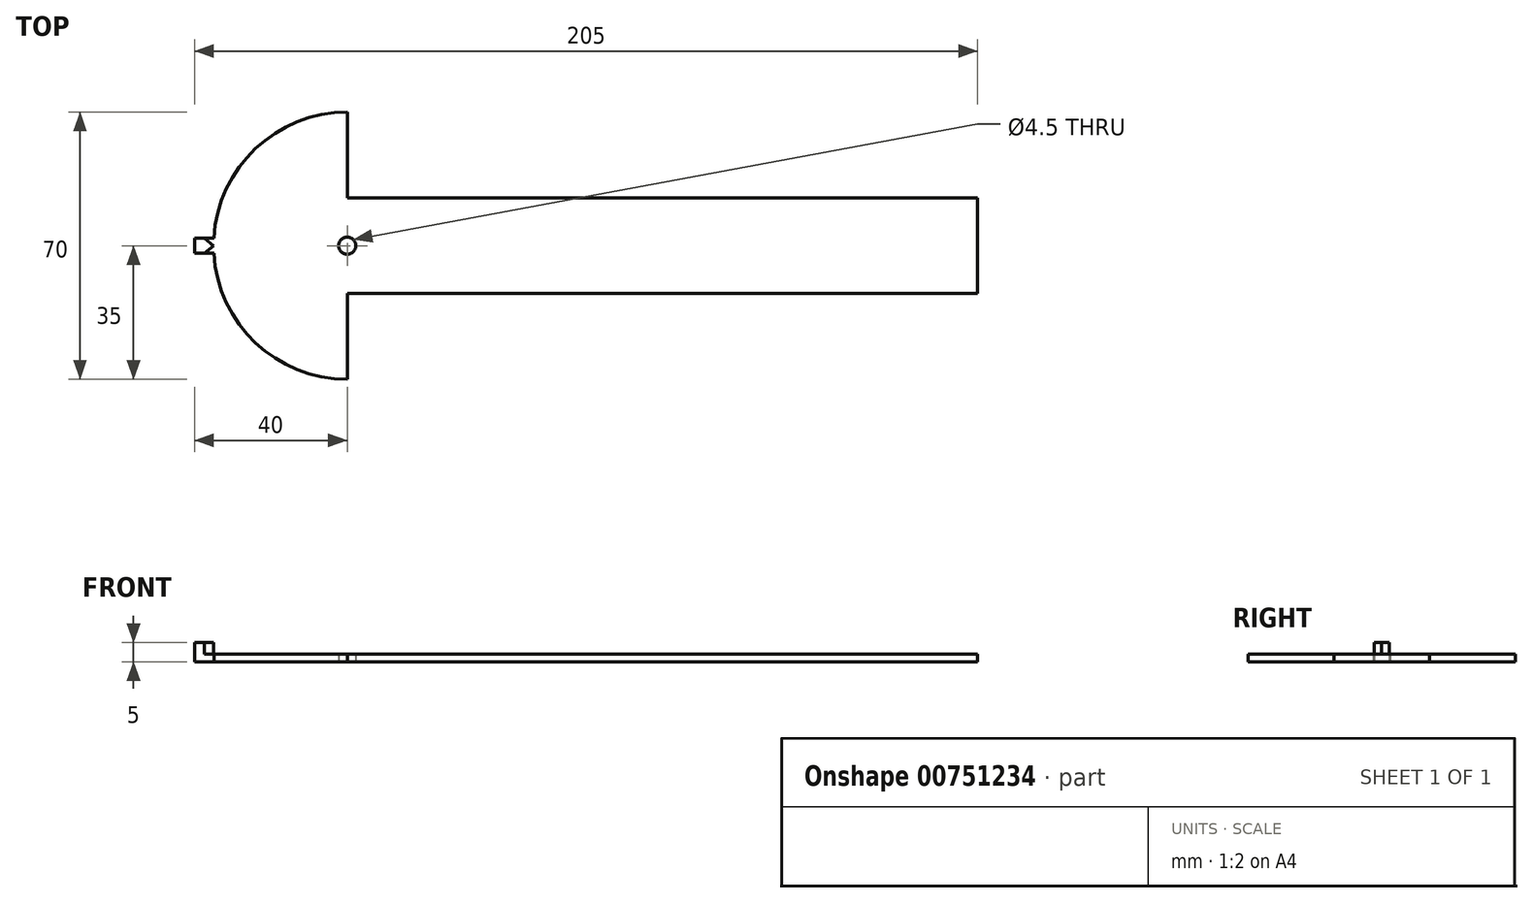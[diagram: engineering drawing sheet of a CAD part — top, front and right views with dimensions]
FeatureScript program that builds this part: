
annotation { "Feature Type Name" : "Feature", "Feature Type Description" : "" }
export const myFeature = defineFeature(function(context is Context, id is Id, definition is map)
    precondition{}
    {
        {
            var Q0;
            Q0=qCreatedBy(makeId("Top.planeOp"),FACE);
            var sketch = newSketch(context, id + "F0", { "sketchPlane" : qUnion([Q0])});
            skLineSegment(sketch, "E0.bottom", {"start": v(-97.7, -12.5) * mm, "end": v(-65, -12.5) * mm, "construction": true});
            skLineSegment(sketch, "E0.top", {"start": v(-97.7, 12.5) * mm, "end": v(-65, 12.5) * mm, "construction": true});
            skLineSegment(sketch, "E0.left", {"start": v(-100, -12.5) * mm, "end": v(-100, 12.5) * mm, "construction": true});
            skLineSegment(sketch, "E0.right", {"start": v(100, -12.5) * mm, "end": v(100, 12.5) * mm});
            skPoint(sketch, "E0.middle", {"position": v(0, 0) * mm});
            skLineSegment(sketch, "E1", {"start": v(-100, 0) * mm, "end": v(100, 0) * mm, "construction": true});
            skLineSegment(sketch, "E2", {"start": v(-65, 35) * mm, "end": v(-65, -35) * mm});
            skPoint(sketch, "E3", {"position": v(-65, 0) * mm});
            skLineSegment(sketch, "E4", {"start": v(-100, 0) * mm, "end": v(-65, 0) * mm, "construction": true});
            skArc(sketch, "E5", {"start": v(-65, 35) * mm, "mid": v(-100, 0) * mm, "end": v(-65, -35) * mm});
            skLineSegment(sketch, "E6", {"start": v(-65, -12.5) * mm, "end": v(100, -12.5) * mm});
            skLineSegment(sketch, "E7", {"start": v(-65, 12.5) * mm, "end": v(100, 12.5) * mm});
            skCircle(sketch, "E8", {"center": v(-65, 0) * mm, "radius": 2.25 * mm});
            skLineSegment(sketch, "E9", {"start": v(-100, 0) * mm, "end": v(-105, 0) * mm, "construction": true});
            skLineSegment(sketch, "E10", {"start": v(-105, 0) * mm, "end": v(-105, -2) * mm});
            skLineSegment(sketch, "E11", {"start": v(-105, -2) * mm, "end": v(-99.94, -2) * mm});
            skLineSegment(sketch, "E12", {"start": v(-100, 0) * mm, "end": v(-102.47, -2) * mm});
            skLineSegment(sketch, "E13.MirrorCS", {"start": v(-105, 2) * mm, "end": v(-99.94, 2) * mm});
            skLineSegment(sketch, "E14.MirrorCS", {"start": v(-105, 0) * mm, "end": v(-105, 2) * mm});
            skLineSegment(sketch, "E15.MirrorCS", {"start": v(-100, 0) * mm, "end": v(-102.47, 2) * mm});
            skLineSegment(sketch, "E16", {"start": v(0, 0) * mm, "end": v(0, -58.7) * mm, "construction": true});
            skSolve(sketch);
        }
        {
            var Q0;
            Q0=makeQuery(id+"F0.imprint","IMPRINT",FACE,{"disambiguationData":[TD([[makeQuery(id+"F0.imprint","IMPRINT",EDGE,{"derivedFrom":sQuery(id+"F0.wireOp",EDGE,"E0.right")}),1.0]])]});
            var Q1;
            {var subQ3=sQuery(id+"F0.wireOp",EDGE,"E12");Q1=makeQuery(id+"F0.imprint","IMPRINT",FACE,{"disambiguationData":[TD([[makeQuery(id+"F0.imprint","IMPRINT",EDGE,{"derivedFrom":subQ3}),1.0]])]});}
            var Q2;
            {var subQ0=sQuery(id+"F0.wireOp",EDGE,"E5");var subQ1=sQuery(id+"F0.wireOp",EDGE,"E2");var subQ8=makeQuery(id+"F0.imprint","INTERSECT",VERTEX,{"disambiguationData":[OD(0.0)],"derivedFrom":[subQ1,subQ0]});Q2=makeQuery(id+"F0.imprint","IMPRINT",FACE,{"disambiguationData":[TD([[makeQuery(id+"F0.imprint","IMPRINT",EDGE,{"disambiguationData":[TD([[subQ8,-1.0]])],"derivedFrom":subQ1}),-1.0]])]});}
            var Q3;
            {var subQ0=sQuery(id+"F0.wireOp",EDGE,"E15.MirrorCS");Q3=makeQuery(id+"F0.imprint","IMPRINT",FACE,{"disambiguationData":[TD([[makeQuery(id+"F0.imprint","IMPRINT",EDGE,{"derivedFrom":subQ0}),-1.0]])]});}
            extrude(context, id + "F1", {"entities" : qUnion([Q0, Q1, Q2, Q3]), "depth" : 2 * mm, "offsetDistance" : 25 * mm});
        }
        {
            var Q0;
            {var subQ5=sQuery(id+"F0.wireOp",EDGE,"E10");Q0=makeQuery(id+"F0.imprint","IMPRINT",FACE,{"disambiguationData":[TD([[makeQuery(id+"F0.imprint","IMPRINT",EDGE,{"derivedFrom":subQ5}),1.0]])]});}
            extrude(context, id + "F2", {"entities" : qUnion([Q0]), "operationType" : NewBodyOperationType.ADD, "depth" : 5 * mm, "offsetDistance" : 25 * mm});
        }
    });
